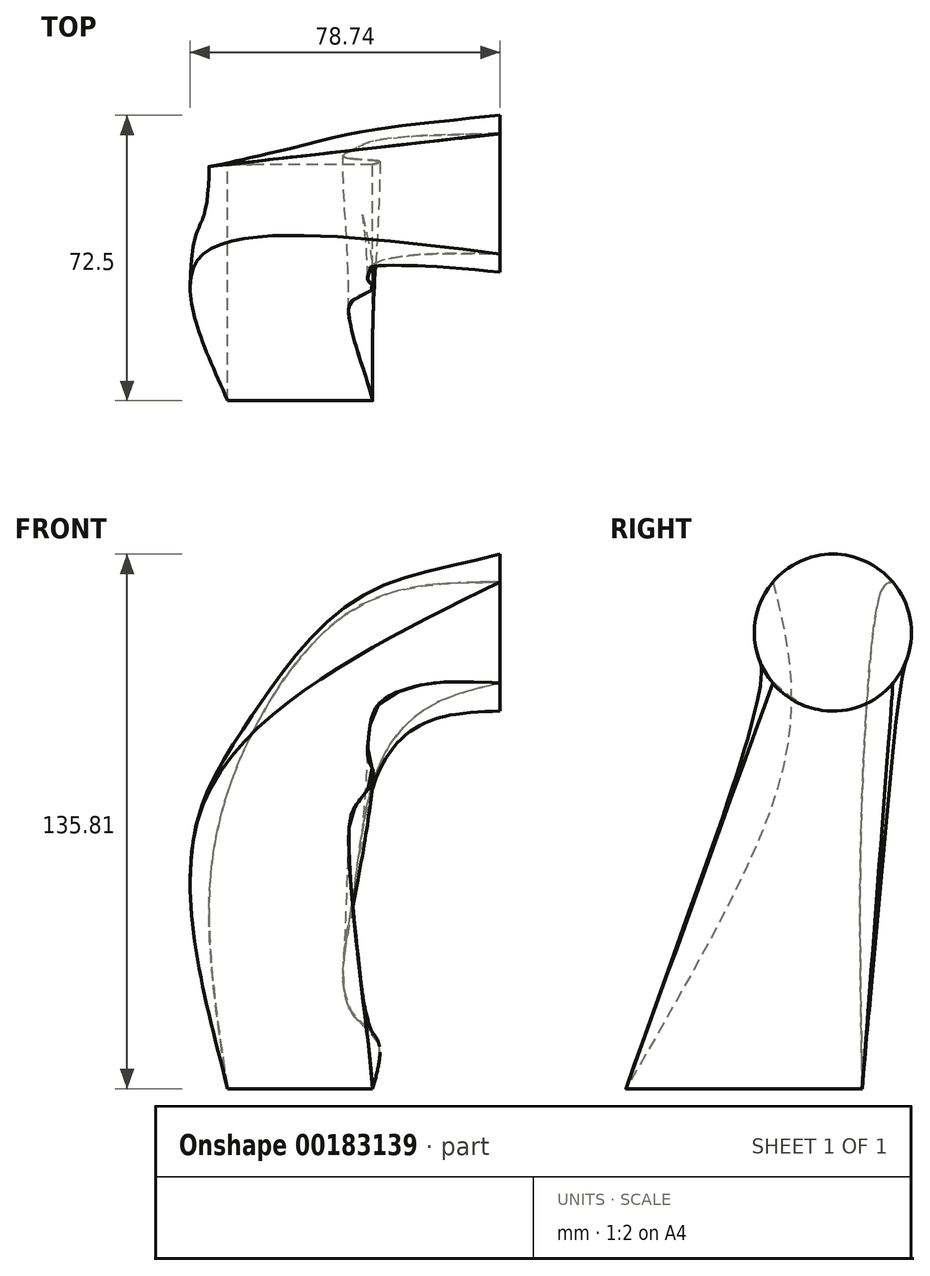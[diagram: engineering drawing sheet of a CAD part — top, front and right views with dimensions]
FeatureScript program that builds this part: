
annotation { "Feature Type Name" : "Feature", "Feature Type Description" : "" }
export const myFeature = defineFeature(function(context is Context, id is Id, definition is map)
    precondition{}
    {
        {
            var Q0;
            Q0=qCreatedBy(makeId("Right.planeOp"),FACE);
            var sketch = newSketch(context, id + "F0", { "sketchPlane" : qUnion([Q0])});
            skArc(sketch, "E0.0", {"start": v(31.49, 128.7) * mm, "mid": v(16.21, 135.81) * mm, "end": v(0.94, 128.7) * mm});
            skArc(sketch, "E0.1", {"start": v(31.49, 103.06) * mm, "mid": v(36.15, 115.87) * mm, "end": v(31.49, 128.7) * mm});
            skArc(sketch, "E0.2", {"start": v(0.94, 103.06) * mm, "mid": v(16.21, 95.94) * mm, "end": v(31.49, 103.06) * mm});
            skArc(sketch, "E0.3", {"start": v(0.94, 128.7) * mm, "mid": v(-3.73, 115.87) * mm, "end": v(0.94, 103.06) * mm});
            skSolve(sketch);
        }
        {
            var Q0;
            Q0=qCreatedBy(makeId("Top.planeOp"),FACE);
            var sketch = newSketch(context, id + "F1", { "sketchPlane" : qUnion([Q0])});
            skLineSegment(sketch, "E1.bottom", {"start": v(-32.36, -36.35) * mm, "end": v(-69.17, -36.35) * mm});
            skLineSegment(sketch, "E1.top", {"start": v(-32.36, 23.67) * mm, "end": v(-69.17, 23.67) * mm});
            skLineSegment(sketch, "E1.left", {"start": v(-32.36, -36.35) * mm, "end": v(-32.36, 23.67) * mm});
            skLineSegment(sketch, "E1.right", {"start": v(-69.17, -36.35) * mm, "end": v(-69.17, 23.67) * mm});
            skSolve(sketch);
        }
        {
            var Q0;
            Q0=sQuery(id+"F0.wireOp",VERTEX,"E0.0.start");
            var Q1;
            Q1=sQuery(id+"F0.wireOp",VERTEX,"E0.1.start");
            var Q2;
            Q2=sQuery(id+"F1.wireOp",VERTEX,"E1.top.end");
            cPlane(context, id + "F2", {"entities" : qUnion([Q0, Q1, Q2]), "cplaneType" : CPlaneType.THREE_POINT, "offset" : 25 * mm, "width" : 150 * mm, "height" : 150 * mm});
        }
        {
            var Q0;
            Q0=qCreatedBy(makeId("Front.planeOp"),FACE);
            var sketch = newSketch(context, id + "F3", { "sketchPlane" : qUnion([Q0])});
            skPoint(sketch, "E2", {"position": v(-76.28, 69.76) * mm});
            skSolve(sketch);
        }
        {
            var Q0;
            Q0=qCreatedBy(id+"F2.planeOp",FACE);
            var sketch = newSketch(context, id + "F4", { "sketchPlane" : qUnion([Q0])});
            skPoint(sketch, "E3.0", {"position": v(3.54, 128.7) * mm});
            skPoint(sketch, "E4.0", {"position": v(-66.07, 0) * mm});
            skFitSpline(sketch, "E5", {"points": [v(3.54, 128.7) * mm, v(-31.95, 122.95) * mm, v(-59.37, 91.27) * mm, v(-70.68, 51.64) * mm, v(-66.07, 0) * mm], "startDerivative": vector(-162.33, -0.35) * mm, "endDerivative": vector(30.35, -193.93) * mm});
            skSolve(sketch);
        }
        {
            var Q0;
            Q0=sQuery(id+"F0.wireOp",VERTEX,"E0.0.end");
            var Q1;
            Q1=sQuery(id+"F3.wireOp",VERTEX,"E2");
            var Q2;
            Q2=sQuery(id+"F1.wireOp",VERTEX,"E1.bottom.end");
            cPlane(context, id + "F5", {"entities" : qUnion([Q0, Q1, Q2]), "cplaneType" : CPlaneType.THREE_POINT, "offset" : 25 * mm, "width" : 150 * mm, "height" : 150 * mm});
        }
        {
            var Q0;
            Q0=qCreatedBy(id+"F5.planeOp",FACE);
            var sketch = newSketch(context, id + "F6", { "sketchPlane" : qUnion([Q0])});
            skPoint(sketch, "E6.0", {"position": v(-17.1, 116.23) * mm});
            skPoint(sketch, "E7.0", {"position": v(63.12, 62.78) * mm});
            skPoint(sketch, "E8.0", {"position": v(55.64, -15.84) * mm});
            skFitSpline(sketch, "E9", {"points": [v(-17.1, 116.23) * mm, v(31.25, 95.77) * mm, v(63.12, 62.78) * mm, v(55.64, -15.84) * mm], "startDerivative": vector(157.66, -57.27) * mm, "endDerivative": vector(-54.06, -226.53) * mm});
            skSolve(sketch);
        }
        {
            var Q0;
            Q0=sQuery(id+"F0.wireOp",VERTEX,"E0.2.start");
            var Q1;
            Q1=sQuery(id+"F6.wireOp",VERTEX,"E8.0");
            var Q2;
            Q2=sQuery(id+"F1.wireOp",VERTEX,"E1.bottom.start");
            cPlane(context, id + "F7", {"entities" : qUnion([Q0, Q1, Q2]), "cplaneType" : CPlaneType.THREE_POINT, "offset" : 25 * mm, "width" : 150 * mm, "height" : 150 * mm});
        }
        {
            var Q0;
            Q0=qCreatedBy(id+"F7.planeOp",FACE);
            var sketch = newSketch(context, id + "F8", { "sketchPlane" : qUnion([Q0])});
            skPoint(sketch, "E10.0", {"position": v(0, 97.23) * mm});
            skPoint(sketch, "E11.0", {"position": v(32.36, -12.37) * mm});
            skFitSpline(sketch, "E12", {"points": [v(0, 97.23) * mm, v(17, 97.23) * mm, v(24.4, 95.41) * mm, v(29.37, 93) * mm, v(32.46, 88.58) * mm, v(33.3, 83.3) * mm, v(33.48, 76.95) * mm, v(32.14, 71.9) * mm, v(35.83, 65.39) * mm, v(38.4, 57.34) * mm, v(33.5, 0) * mm, v(32.36, -12.37) * mm], "startDerivative": vector(160.97, 6.89) * mm, "endDerivative": vector(-6.37, -86.84) * mm});
            skSolve(sketch);
        }
        {
            var Q0;
            Q0=sQuery(id+"F0.wireOp",VERTEX,"E0.1.start");
            var Q1;
            Q1=sQuery(id+"F1.wireOp",VERTEX,"E1.top.start");
            var Q2;
            Q2=sQuery(id+"F4.wireOp",VERTEX,"E4.0");
            cPlane(context, id + "F9", {"entities" : qUnion([Q0, Q1, Q2]), "cplaneType" : CPlaneType.THREE_POINT, "offset" : 25 * mm, "width" : 150 * mm, "height" : 150 * mm});
        }
        {
            var Q0;
            Q0=qCreatedBy(id+"F9.planeOp",FACE);
            var sketch = newSketch(context, id + "F10", { "sketchPlane" : qUnion([Q0])});
            skPoint(sketch, "E13.0", {"position": v(0, 105.15) * mm});
            skPoint(sketch, "E14.0", {"position": v(-32.36, 1.8) * mm});
            skFitSpline(sketch, "E15", {"points": [v(0, 105.15) * mm, v(-18.46, 98.86) * mm, v(-31.23, 82.93) * mm, v(-37.31, 51.02) * mm, v(-39.88, 31.72) * mm, v(-37, 20.24) * mm, v(-31.1, 14.15) * mm, v(-32.36, 1.8) * mm], "startDerivative": vector(-128.14, -29.51) * mm, "endDerivative": vector(-32.22, -115.55) * mm});
            skSolve(sketch);
        }
        {
            var Q0;
            Q0=sQuery(id+"F4.wireOp",EDGE,"E5");
            var Q1;
            Q1=sQuery(id+"F6.wireOp",EDGE,"E9");
            var Q2;
            Q2=makeQuery(id+"F0.imprint","IMPRINT",FACE,{"disambiguationData":[TD([[makeQuery(id+"F0.imprint","IMPRINT",EDGE,{"derivedFrom":sQuery(id+"F0.wireOp",EDGE,"E0.0")}),1.0]])]});
            var Q3;
            Q3=makeQuery(id+"F1.imprint","IMPRINT",FACE,{"disambiguationData":[TD([[makeQuery(id+"F1.imprint","IMPRINT",EDGE,{"derivedFrom":sQuery(id+"F1.wireOp",EDGE,"E1.bottom")}),-1.0]])]});
            var Q4;
            Q4=sQuery(id+"F4.wireOp",EDGE,"E5");
            var Q5;
            Q5=sQuery(id+"F6.wireOp",EDGE,"E9");
            var Q6;
            Q6=sQuery(id+"F10.wireOp",EDGE,"E15");
            var Q7;
            Q7=sQuery(id+"F8.wireOp",EDGE,"E12");
            loft(context, id + "F11", {"spine" : qUnion([Q0, Q1]), "addGuides" : true, "sheetProfilesArray" : [{ "sheetProfileEntities" : qUnion([Q2]) }, { "sheetProfileEntities" : qUnion([Q3]) }], "guidesArray" : [{ "guideEntities" : qUnion([Q4]), "guideDerivativeType" : LoftGuideDerivativeType.DEFAULT, "guideDerivativeMagnitude" : 1 }, { "guideEntities" : qUnion([Q5]), "guideDerivativeType" : LoftGuideDerivativeType.DEFAULT, "guideDerivativeMagnitude" : 1 }, { "guideEntities" : qUnion([Q6]), "guideDerivativeType" : LoftGuideDerivativeType.DEFAULT, "guideDerivativeMagnitude" : 1 }, { "guideEntities" : qUnion([Q7]), "guideDerivativeType" : LoftGuideDerivativeType.DEFAULT, "guideDerivativeMagnitude" : 1 }]});
        }
        {
            var Q0;
            Q0=makeQuery(id+"F11.opLoft","SWEPT_EDGE",EDGE,{"disambiguationData":[OSD([sQuery(id+"F0.wireOp",EDGE,"E0.2"),sQuery(id+"F0.wireOp",EDGE,"E0.3"),sQuery(id+"F1.wireOp",EDGE,"E1.bottom"),sQuery(id+"F1.wireOp",EDGE,"E1.left")])]});
            var Q1;
            Q1=makeQuery(id+"F11.opLoft","SWEPT_EDGE",EDGE,{"disambiguationData":[OSD([sQuery(id+"F0.wireOp",EDGE,"E0.1"),sQuery(id+"F0.wireOp",EDGE,"E0.2"),sQuery(id+"F1.wireOp",EDGE,"E1.top"),sQuery(id+"F1.wireOp",EDGE,"E1.left")])]});
            var Q2;
            Q2=makeQuery(id+"F11.opLoft","SWEPT_EDGE",EDGE,{"disambiguationData":[OSD([sQuery(id+"F4.wireOp",EDGE,"E5")])]});
            fillet(context, id + "F12", {"entities" : qUnion([Q0, Q1, Q2]), "radius" : 0.02 * mm, "tangentPropagation" : true, "allowEdgeOverflow" : false});
        }
    });
